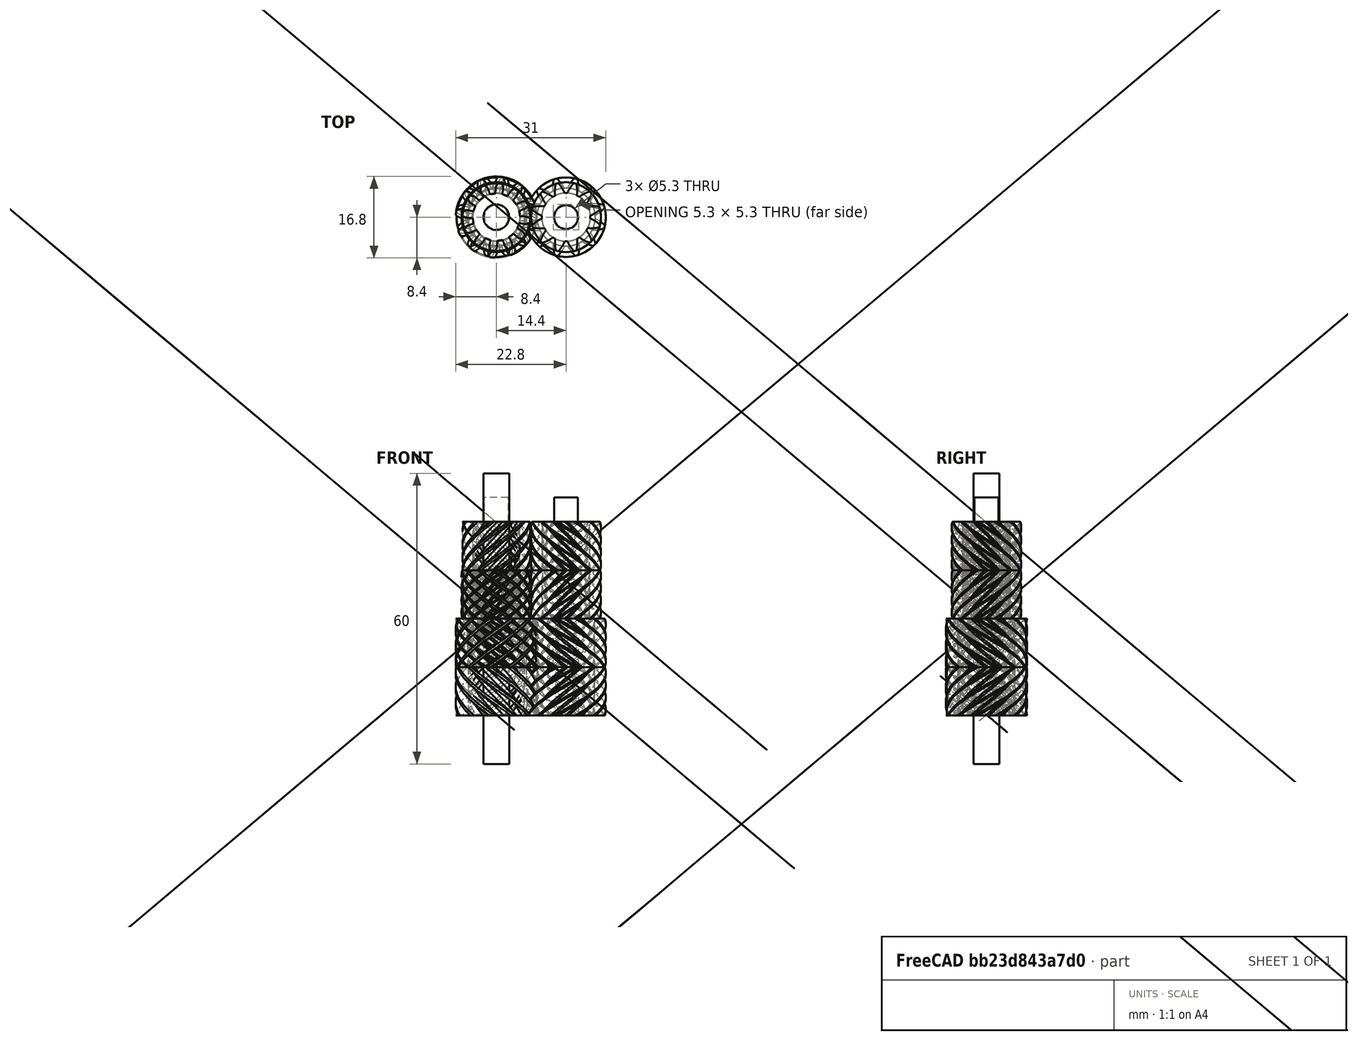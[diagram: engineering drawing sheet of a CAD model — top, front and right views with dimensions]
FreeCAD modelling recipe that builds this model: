
FCSTD DOCUMENT  (FreeCAD 0.19R24276 (Git))
Label: G-midi_outer-gear_001
License: All rights reserved
LicenseURL: http://en.wikipedia.org/wiki/All_rights_reserved
objects: Part::FeaturePython×8, Part::Cylinder×8, Part::Cut×5, Part::Compound×2, Mesh::Feature×1
note: 23 computed .brp shape members not serialized (recipe doc carries the construction recipe); baked Part::Feature solids carry a one-line shape summary decoded from their .brp

FEATURE [Part::FeaturePython] wormgear031  # WARN: FeaturePython — macro-defined, semantics opaque (R4)
  AttacherType = Attacher::AttachEngine3D
  Placement = pos=(14.4,0,-10) rot=(0,0,1;0.991347rad)
  beta = 34.439
  clearance = 0.25
  diameter = 14
  head = 0.5
  height = 10
  module = 0.8
  pressure_angle = 20
  reverse_pitch = false
  teeth = 12
  version = 0.0.3
FEATURE [Part::FeaturePython] wormgear025  # WARN: FeaturePython — macro-defined, semantics opaque (R4)
  AttacherType = Attacher::AttachEngine3D
  Placement = pos=(14.4,0,0) rot=(0,0,1;0.977384rad)
  beta = 34.439
  clearance = 0.25
  diameter = 14
  head = 0.5
  height = 10
  module = 0.8
  pressure_angle = 20
  reverse_pitch = true
  teeth = 12
  version = 0.0.3
FEATURE [Part::FeaturePython] wormgear033  # WARN: FeaturePython — macro-defined, semantics opaque (R4)
  AttacherType = Attacher::AttachEngine3D
  Placement = pos=(14.4,0,10) rot=(0,0,1;0.977384rad)
  beta = 38.6598
  clearance = 0.25
  diameter = 12
  head = 0.5
  height = 10
  module = 0.8
  pressure_angle = 20
  reverse_pitch = false
  teeth = 12
  version = 0.0.3
FEATURE [Part::FeaturePython] wormgear032  # WARN: FeaturePython — macro-defined, semantics opaque (R4)
  AttacherType = Attacher::AttachEngine3D
  Placement = pos=(14.4,0,20) rot=(0,0,1;0.968658rad)
  beta = 38.6598
  clearance = 0.25
  diameter = 12
  head = 0.5
  height = 10
  module = 0.8
  pressure_angle = 20
  reverse_pitch = true
  teeth = 12
  version = 0.0.3
FEATURE [Part::Cylinder] Cylinder017  label="Válec017"
  Angle = 360
  AttacherType = Attacher::AttachEngine3D
  Height = 60
  Placement = pos=(14.4,0,-20) rot=(0,0,1;0rad)
  Radius = 2.65
FEATURE [Part::Cut] Cut317
  Base = -> wormgear031
  Tool = -> Cylinder017
FEATURE [Part::Cylinder] Cylinder025  label="Válec025"
  Angle = 360
  AttacherType = Attacher::AttachEngine3D
  Height = 5
  Placement = pos=(14.4,0,30) rot=(0,0,1;0rad)
  Radius = 2.45
FEATURE [Part::Cylinder] Cylinder016  label="Válec016"
  Angle = 360
  AttacherType = Attacher::AttachEngine3D
  Height = 60
  Placement = pos=(14.4,0,-20) rot=(0,0,1;0rad)
  Radius = 2.65
FEATURE [Part::Cut] Cut314
  Base = -> wormgear025
  Tool = -> Cylinder016
FEATURE [Part::Cylinder] Cylinder018  label="Válec018"
  Angle = 360
  AttacherType = Attacher::AttachEngine3D
  Height = 20
  Placement = pos=(14.4,0,-20) rot=(0,0,1;0rad)
  Radius = 2.65
FEATURE [Part::Cut] Cut316
  Base = -> wormgear032
  Tool = -> Cylinder018
FEATURE [Part::Cylinder] Cylinder019  label="Válec019"
  Angle = 360
  AttacherType = Attacher::AttachEngine3D
  Height = 60
  Placement = pos=(14.4,0,40) rot=(0,0,1;0rad)
  Radius = 2.65
FEATURE [Part::Cut] Cut313
  Base = -> wormgear033
  Tool = -> Cylinder019
FEATURE [Part::Compound] Compound539  label="gearovina_midi_vnejskove"
  Links = -> [Cylinder025,Cut313,Cut316,Cut314,Cut317]
FEATURE [Part::FeaturePython] cycloidgear  # WARN: FeaturePython — macro-defined, semantics opaque (R4)
  AttacherType = Attacher::AttachEngine3D
  Placement = pos=(0,0,10) rot=(0,0,1;0rad)
  backlash = 0
  beta = 50
  clearance = 0.25
  double_helix = true
  height = 20
  inner_diameter = 5
  module = 1
  numpoints = 15
  outer_diameter = 5
  teeth = 12
  version = 0.0.3
FEATURE [Part::FeaturePython] wormgear034  # WARN: FeaturePython — macro-defined, semantics opaque (R4)
  AttacherType = Attacher::AttachEngine3D
  Placement = pos=(0,0,10) rot=(0,0,1;0.977384rad)
  beta = 38.6598
  clearance = 0.25
  diameter = 12
  head = 0.5
  height = 10
  module = 0.8
  pressure_angle = 20
  reverse_pitch = false
  teeth = 12
  version = 0.0.3
FEATURE [Part::FeaturePython] cycloidgear001  # WARN: FeaturePython — macro-defined, semantics opaque (R4)
  AttacherType = Attacher::AttachEngine3D
  Placement = pos=(0,0,-10) rot=(0,0,1;0.331613rad)
  backlash = 0
  beta = 50
  clearance = 0.25
  double_helix = true
  height = 20
  inner_diameter = 5
  module = 1.2
  numpoints = 15
  outer_diameter = 5
  teeth = 12
  version = 0.0.3
FEATURE [Part::FeaturePython] wormgear035  # WARN: FeaturePython — macro-defined, semantics opaque (R4)
  AttacherType = Attacher::AttachEngine3D
  Placement = pos=(0,0,0) rot=(0,0,1;0.977384rad)
  beta = 34.439
  clearance = 0.25
  diameter = 14
  head = 0.5
  height = 10
  module = 0.8
  pressure_angle = 20
  reverse_pitch = true
  teeth = 12
  version = 0.0.3
FEATURE [Part::Cylinder] Cylinder026  label="Válec026"
  Angle = 360
  AttacherType = Attacher::AttachEngine3D
  Height = 5
  Placement = pos=(0,0,30) rot=(0,0,1;0rad)
  Radius = 2.45
FEATURE [Part::Cylinder] Cylinder027  label="Válec027"
  Angle = 360
  AttacherType = Attacher::AttachEngine3D
  Height = 60
  Placement = pos=(0,0,-20) rot=(0,0,1;0rad)
  Radius = 2.65
FEATURE [Part::Cylinder] Cylinder028  label="Válec028"
  Angle = 360
  AttacherType = Attacher::AttachEngine3D
  Height = 60
  Placement = pos=(0,0,-20) rot=(0,0,1;0rad)
  Radius = 2.65
FEATURE [Part::Cut] Cut
  Base = -> cycloidgear001
  Tool = -> Cylinder027
FEATURE [Part::Compound] Compound  label="G-midi_outer-gear"
  Links = -> [Cut,Cylinder026,cycloidgear]
FEATURE [Mesh::Feature] Mesh  label="G-midi_outer-gear (Meshed)"
